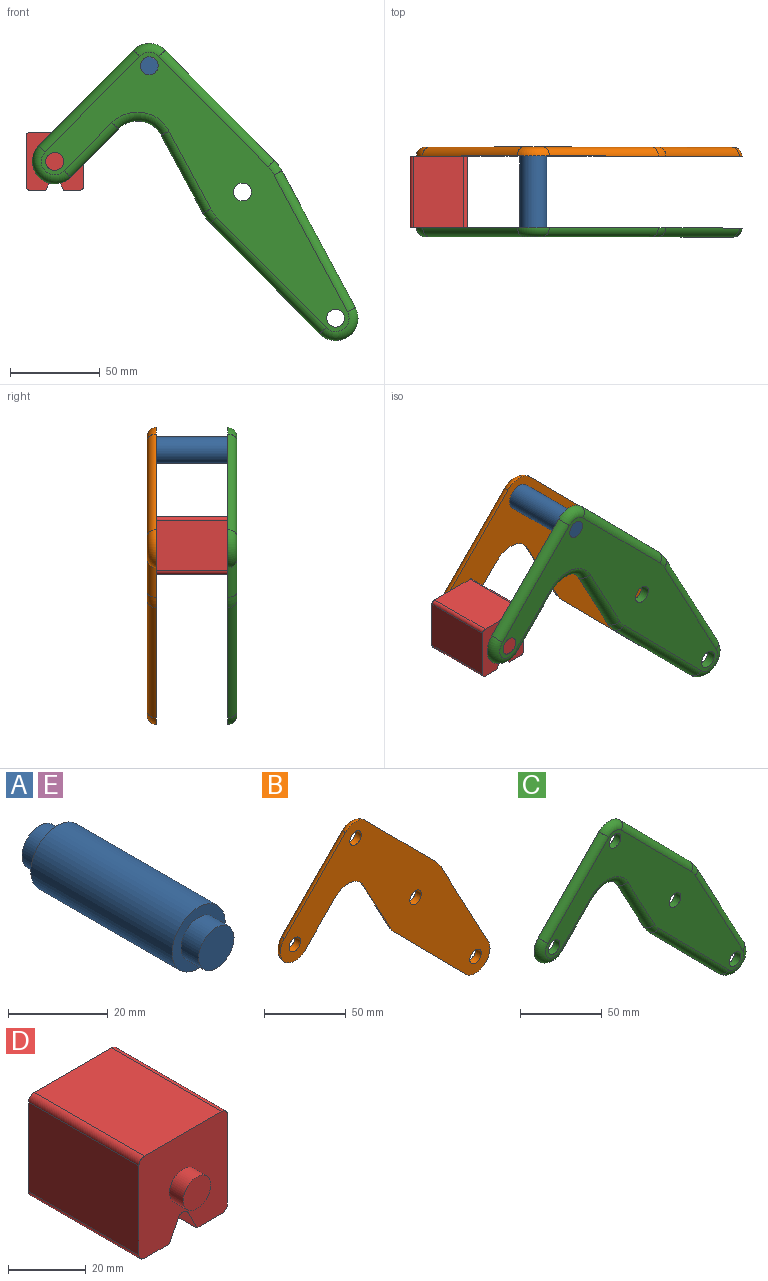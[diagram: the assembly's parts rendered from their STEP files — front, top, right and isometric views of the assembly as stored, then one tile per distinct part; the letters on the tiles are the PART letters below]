
ASSEMBLY  parts=5 mates=1
PART A: 7 faces, bbox 15x50x15 mm
  f0: cylinder r=7.5mm len=40mm, axis (0,-1,0), area 1885mm2, adj f2,f5
  f1: cylinder r=5mm len=10mm, axis (0,1,0), area 157.1mm2, adj f2,f3
  f2: plane 15x15mm, normal (0,-1,0), area 98.2mm2, adj f0,f1
  f3: plane 10x10mm, normal (0,-1,0), area 78.5mm2, adj f1
  f4: cylinder r=5mm len=10mm, axis (0,-1,0), area 157.1mm2, adj f5,f6
  f5: plane 15x15mm, normal (0,1,0), area 98.2mm2, adj f0,f4
  f6: plane 10x10mm, normal (0,1,0), area 78.5mm2, adj f4
PART B: 18 faces, bbox 183.7x5x167.8 mm
  f0: cylinder r=5mm len=10mm, axis (0,-1,0), area 157.1mm2, adj f4,f5
  f1: cylinder r=5mm len=10mm, axis (0,-1,0), area 157.1mm2, adj f4,f5
  f2: cylinder r=5mm len=10mm, axis (0,-1,0), area 157.1mm2, adj f4,f5
  f3: cylinder r=5mm len=10mm, axis (0,-1,0), area 157.1mm2, adj f4,f5
  f4: plane 171.66x155.78mm, normal (0,1,0), area 5993.5mm2, adj f0,f1,f2,f3,f6,f7,f8,f9
  f5: plane 181.66x165.78mm, normal (0,-1,0), area 8710.1mm2, adj f0,f1,f2,f3,f6,f7,f8,f9
  f6: torus R=7.5mm, axis (0,1,0), area 132.8mm2, adj f4,f5,f7,f8
  f7: cylinder r=5mm len=56.87mm, axis (0.7,0,0.71), area 589mm2, adj f4,f5,f6,f9
  f8: cylinder r=5mm len=65.12mm, axis (0.7,0,-0.71), area 680.2mm2, adj f4,f5,f6,f10
  f9: torus R=7.5mm, axis (0,1,0), area 263.6mm2, adj f4,f5,f7,f11
  f10: torus R=20mm, axis (0,1,0), area 52.2mm2, adj f4,f5,f8,f12
  f11: cylinder r=5mm len=30.37mm, axis (-0.7,0,-0.71), area 296.5mm2, adj f4,f5,f9,f13
  f12: cylinder r=5mm len=78.67mm, axis (0.47,0,-0.88), area 680.2mm2, adj f4,f5,f10,f14
  f13: torus R=20mm, axis (0,1,0), area 246.9mm2, adj f4,f5,f11,f15
  f14: torus R=7.5mm, axis (0,1,0), area 239.5mm2, adj f4,f5,f12,f16
  f15: cylinder r=5mm len=45.85mm, axis (-0.47,0,0.88), area 387.7mm2, adj f4,f5,f13,f17
  f16: cylinder r=5mm len=65.12mm, axis (-0.7,0,0.71), area 680.2mm2, adj f4,f5,f14,f17
  f17: torus R=20mm, axis (0,1,0), area 52.2mm2, adj f4,f5,f15,f16
PART C: 18 faces, bbox 183.7x8.6x167.8 mm
  f0: cylinder r=5mm len=10mm, axis (0,1,0), area 157.1mm2, adj f4,f5
  f1: cylinder r=5mm len=10mm, axis (0,1,0), area 157.1mm2, adj f4,f5
  f2: cylinder r=5mm len=10mm, axis (0,1,0), area 157.1mm2, adj f4,f5
  f3: cylinder r=5mm len=10mm, axis (0,1,0), area 157.1mm2, adj f4,f5
  f4: plane 171.66x155.78mm, normal (0,-1,0), area 5993.5mm2, adj f0,f1,f2,f3,f6,f7,f8,f9
  f5: plane 181.66x165.78mm, normal (0,1,0), area 8710.1mm2, adj f0,f1,f2,f3,f6,f7,f8,f9
  f6: torus R=7.5mm, axis (0,-1,0), area 132.8mm2, adj f4,f5,f7,f8
  f7: cylinder r=5mm len=56.87mm, axis (0.7,0,0.71), area 589mm2, adj f4,f5,f6,f9
  f8: cylinder r=5mm len=65.12mm, axis (0.7,0,-0.71), area 680.2mm2, adj f4,f5,f6,f10
  f9: torus R=7.5mm, axis (0,-1,0), area 263.6mm2, adj f4,f5,f7,f11
  f10: torus R=20mm, axis (0,-1,0), area 52.2mm2, adj f4,f5,f8,f12
  f11: cylinder r=5mm len=30.37mm, axis (-0.7,0,-0.71), area 296.5mm2, adj f4,f5,f9,f13
  f12: cylinder r=5mm len=78.67mm, axis (0.47,0,-0.88), area 680.2mm2, adj f4,f5,f10,f14
  f13: torus R=20mm, axis (0,-1,0), area 246.9mm2, adj f4,f5,f11,f15
  f14: torus R=7.5mm, axis (0,-1,0), area 239.5mm2, adj f4,f5,f12,f16
  f15: cylinder r=5mm len=45.85mm, axis (-0.47,0,0.88), area 387.7mm2, adj f4,f5,f13,f17
  f16: cylinder r=5mm len=65.12mm, axis (-0.7,0,0.71), area 680.2mm2, adj f4,f5,f14,f17
  f17: torus R=20mm, axis (0,-1,0), area 52.2mm2, adj f4,f5,f15,f16
PART D: 18 faces, bbox 32.1x50x32.1 mm
  f0: plane 40x28.08mm, normal (1,0,0), area 1123.1mm2, adj f4,f10,f13,f14
  f1: plane 40x9.04mm, normal (0,0,-1), area 361.6mm2, adj f2,f4,f10,f14
  f2: plane 40x6.42mm, normal (-0.89,0,-0.45), area 287.2mm2, adj f1,f4,f10,f15
  f3: plane 40x6.42mm, normal (0.89,0,-0.45), area 287.2mm2, adj f4,f5,f10,f15
  f4: plane 32.08x32.08mm, normal (0,-1,0), area 900.6mm2, adj f0,f1,f2,f3,f5,f6,f7,f9
  f5: plane 40x9.04mm, normal (0,0,-1), area 361.6mm2, adj f3,f4,f10,f16
  f6: plane 40x28.08mm, normal (0,0,1), area 1123.1mm2, adj f4,f10,f13,f17
  f7: plane 40x28.08mm, normal (-1,0,0), area 1123.1mm2, adj f4,f10,f16,f17
  f8: plane 10x10mm, normal (0,-1,0), area 78.5mm2, adj f9
  f9: cylinder r=5mm len=10mm, axis (0,1,0), area 157.1mm2, adj f4,f8
  f10: plane 32.08x32.08mm, normal (0,1,0), area 900.6mm2, adj f0,f1,f2,f3,f5,f6,f7,f12
  f11: plane 10x10mm, normal (0,1,0), area 78.5mm2, adj f12
  f12: cylinder r=5mm len=10mm, axis (0,-1,0), area 157.1mm2, adj f10,f11
  f13: cylinder r=2mm len=40mm, axis (0,1,0), area 125.7mm2, adj f0,f4,f6,f10
  f14: cylinder r=2mm len=40mm, axis (0,-1,0), area 125.7mm2, adj f0,f1,f4,f10
  f15: cylinder r=2mm len=40mm, axis (0,1,0), area 177.1mm2, adj f2,f3,f4,f10
  f16: cylinder r=2mm len=40mm, axis (0,1,0), area 125.7mm2, adj f4,f5,f7,f10
  f17: cylinder r=2mm len=40mm, axis (0,-1,0), area 125.7mm2, adj f4,f6,f7,f10
PART E: same geometry as A
PLACE A at identity
PLACE B t=(0,-40,0)mm
PLACE C at identity fixed
PLACE D at identity
PLACE E at identity
MATE fastened B.f2 <-> A.f0  axis (0,-1,0) through (-51.98,40,70.39)mm
